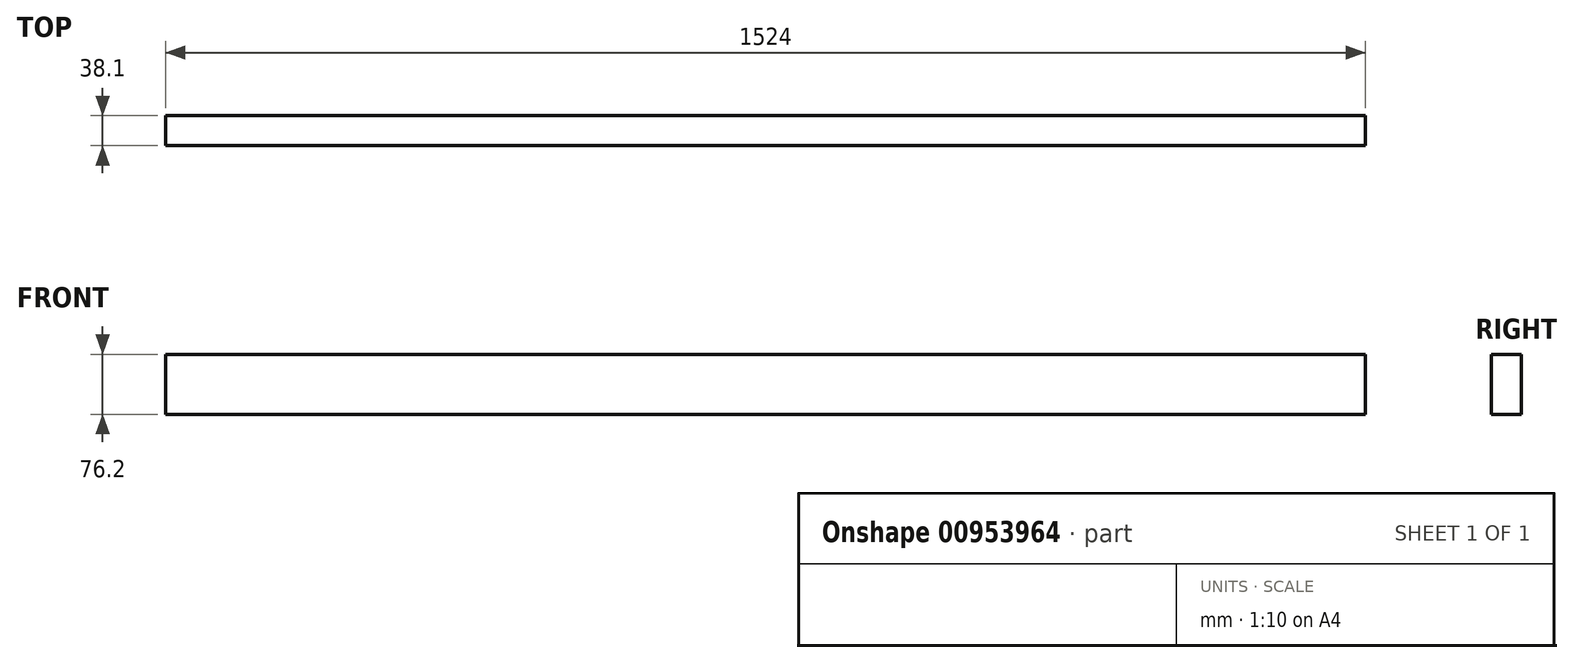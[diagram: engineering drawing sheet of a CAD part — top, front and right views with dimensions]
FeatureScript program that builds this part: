
annotation { "Feature Type Name" : "Feature", "Feature Type Description" : "" }
export const myFeature = defineFeature(function(context is Context, id is Id, definition is map)
    precondition{}
    {
        {
            var Q0;
            Q0=qCreatedBy(makeId("Front.planeOp"),FACE);
            var sketch = newSketch(context, id + "F0", { "sketchPlane" : qUnion([Q0])});
            skLineSegment(sketch, "E0.bottom", {"start": v(0, 0) * mm, "end": v(1524, 0) * mm});
            skLineSegment(sketch, "E0.top", {"start": v(0, 76.2) * mm, "end": v(1524, 76.2) * mm});
            skLineSegment(sketch, "E0.left", {"start": v(0, 0) * mm, "end": v(0, 76.2) * mm});
            skLineSegment(sketch, "E0.right", {"start": v(1524, 0) * mm, "end": v(1524, 76.2) * mm});
            skSolve(sketch);
        }
        {
            var Q0;
            Q0=makeQuery(id+"F0.imprint","IMPRINT",FACE,{"disambiguationData":[TD([[makeQuery(id+"F0.imprint","IMPRINT",EDGE,{"derivedFrom":sQuery(id+"F0.wireOp",EDGE,"E0.bottom")}),1.0]])]});
            extrude(context, id + "F1", {"entities" : qUnion([Q0]), "depth" : 38.1 * mm, "offsetDistance" : 25.4 * mm});
        }
    });
